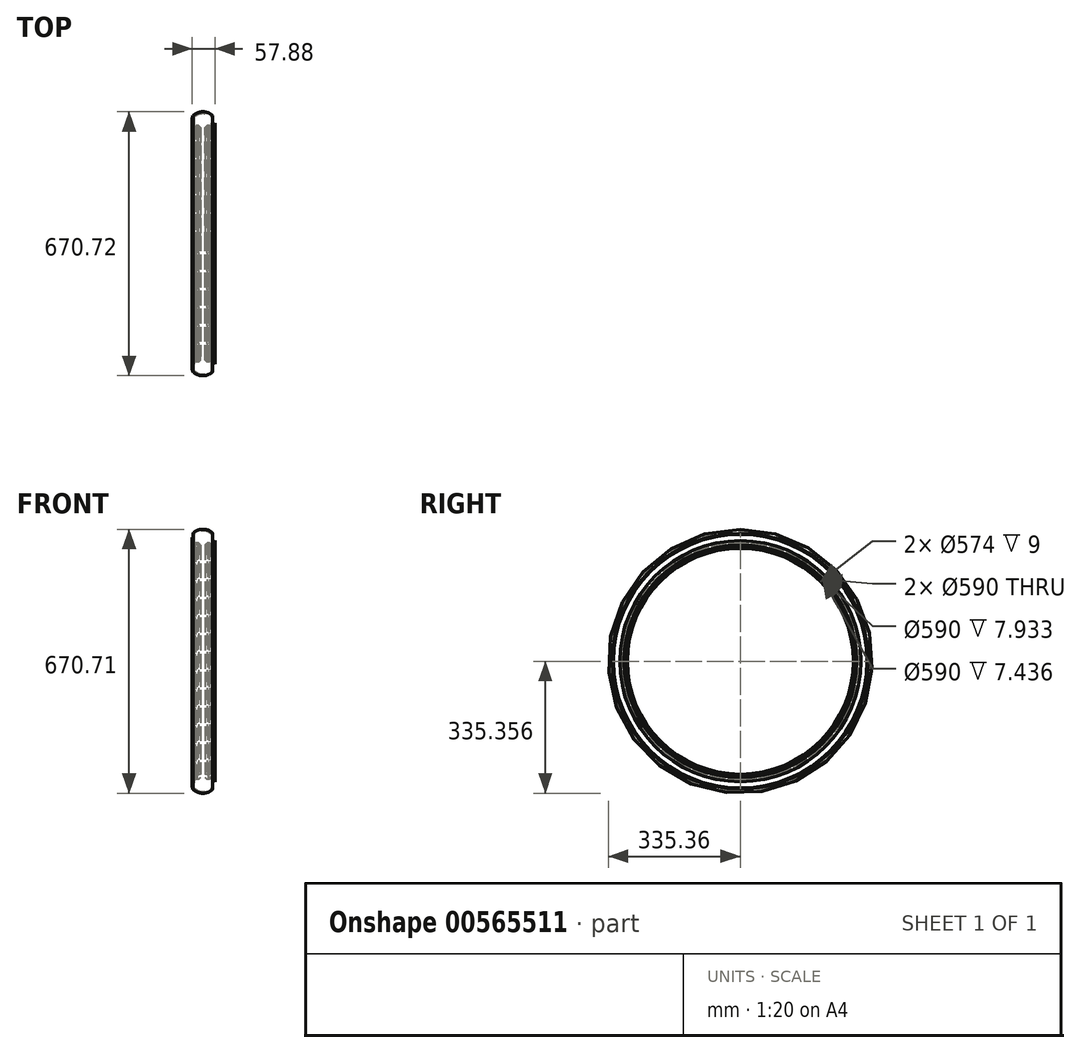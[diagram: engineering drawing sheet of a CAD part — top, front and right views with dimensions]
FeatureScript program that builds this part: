
annotation { "Feature Type Name" : "Feature", "Feature Type Description" : "" }
export const myFeature = defineFeature(function(context is Context, id is Id, definition is map)
    precondition{}
    {
        {
            var Q0;
            Q0=qCreatedBy(makeId("Front.planeOp"),FACE);
            var sketch = newSketch(context, id + "F0", { "sketchPlane" : qUnion([Q0])});
            skLineSegment(sketch, "E0", {"start": v(-253.23, -259.64) * mm, "end": v(-183.54, -259.64) * mm, "construction": true});
            skArc(sketch, "E1", {"start": v(-228.23, 65.36) * mm, "mid": v(-253.23, 75.71) * mm, "end": v(-278.23, 65.36) * mm});
            skLineSegment(sketch, "E2", {"start": v(-278.23, 65.36) * mm, "end": v(-228.23, 65.36) * mm, "construction": true});
            skLineSegment(sketch, "E3", {"start": v(-270.34, 40.36) * mm, "end": v(-264.23, 40.36) * mm});
            skLineSegment(sketch, "E4", {"start": v(-273.23, 35.36) * mm, "end": v(-265.23, 35.36) * mm});
            skLineSegment(sketch, "E5", {"start": v(-253.23, 40.36) * mm, "end": v(-253.23, 35.36) * mm, "construction": true});
            skArc(sketch, "E6.0", {"start": v(-231.06, 62.53) * mm, "mid": v(-253.23, 71.71) * mm, "end": v(-275.4, 62.53) * mm});
            skLineSegment(sketch, "E7", {"start": v(-231.06, 62.53) * mm, "end": v(-228.23, 65.36) * mm});
            skLineSegment(sketch, "E8", {"start": v(-231.06, 62.53) * mm, "end": v(-226.37, 57.84) * mm, "construction": true});
            skLineSegment(sketch, "E9.0.MirrorCS", {"start": v(-275.4, 62.53) * mm, "end": v(-278.23, 65.36) * mm});
            skLineSegment(sketch, "E10", {"start": v(-273.23, 35.36) * mm, "end": v(-270.34, 40.36) * mm});
            skPoint(sketch, "E11.start.orphan", {"position": v(-265.73, 40.36) * mm});
            skLineSegment(sketch, "E12", {"start": v(-265.23, 35.36) * mm, "end": v(-265.23, 30.36) * mm});
            skLineSegment(sketch, "E13", {"start": v(-265.23, 30.36) * mm, "end": v(-268.23, 30.36) * mm});
            skLineSegment(sketch, "E14", {"start": v(-268.23, 30.36) * mm, "end": v(-268.23, 27.36) * mm});
            skLineSegment(sketch, "E15", {"start": v(-268.23, 27.36) * mm, "end": v(-259.23, 27.36) * mm});
            skLineSegment(sketch, "E16", {"start": v(-259.23, 27.36) * mm, "end": v(-259.23, 35.36) * mm});
            skLineSegment(sketch, "E17", {"start": v(-259.23, 35.36) * mm, "end": v(-264.23, 40.36) * mm});
            skLineSegment(sketch, "E18.0.MirrorCS", {"start": v(-233.23, 35.36) * mm, "end": v(-236.11, 40.36) * mm});
            skLineSegment(sketch, "E18.1.MirrorCS", {"start": v(-241.23, 35.36) * mm, "end": v(-241.23, 30.36) * mm});
            skLineSegment(sketch, "E18.2.MirrorCS", {"start": v(-241.23, 30.36) * mm, "end": v(-238.23, 30.36) * mm});
            skPoint(sketch, "E18.3.MirrorP", {"position": v(-240.73, 40.36) * mm});
            skLineSegment(sketch, "E18.4.MirrorCS", {"start": v(-236.11, 40.36) * mm, "end": v(-242.23, 40.36) * mm});
            skLineSegment(sketch, "E18.5.MirrorCS", {"start": v(-238.23, 27.36) * mm, "end": v(-247.23, 27.36) * mm});
            skLineSegment(sketch, "E18.6.MirrorCS", {"start": v(-247.23, 35.36) * mm, "end": v(-242.23, 40.36) * mm});
            skLineSegment(sketch, "E18.7.MirrorCS", {"start": v(-238.23, 30.36) * mm, "end": v(-238.23, 27.36) * mm});
            skLineSegment(sketch, "E18.8.MirrorCS", {"start": v(-247.23, 27.36) * mm, "end": v(-247.23, 35.36) * mm});
            skLineSegment(sketch, "E19.0.MirrorCS", {"start": v(-233.23, 35.36) * mm, "end": v(-241.23, 35.36) * mm});
            skSolve(sketch);
        }
        {
            var Q0;
            Q0=makeQuery(id+"F0.imprint","IMPRINT",FACE,{"disambiguationData":[TD([[makeQuery(id+"F0.imprint","IMPRINT",EDGE,{"derivedFrom":sQuery(id+"F0.wireOp",EDGE,"E1")}),1.0]])]});
            var Q1;
            Q1=makeQuery(id+"F0.imprint","IMPRINT",FACE,{"disambiguationData":[TD([[makeQuery(id+"F0.imprint","IMPRINT",EDGE,{"derivedFrom":sQuery(id+"F0.wireOp",EDGE,"E18.0.MirrorCS")}),1.0]])]});
            var Q2;
            Q2=makeQuery(id+"F0.imprint","IMPRINT",FACE,{"disambiguationData":[TD([[makeQuery(id+"F0.imprint","IMPRINT",EDGE,{"derivedFrom":sQuery(id+"F0.wireOp",EDGE,"E3")}),-1.0]])]});
            var Q3;
            Q3=sQuery(id+"F0.wireOp",EDGE,"E0");
            revolve(context, id + "F1", {"entities" : qUnion([Q0, Q1, Q2]), "axis" : qUnion([Q3]), "revolveType" : RevolveType.FULL});
        }
        {
            var Q0;
            Q0=qCreatedBy(makeId("Front.planeOp"),FACE);
            var sketch = newSketch(context, id + "F2", { "sketchPlane" : qUnion([Q0])});
            skArc(sketch, "E20", {"start": v(-233.83, 35.31) * mm, "mid": v(-222.2, 49.33) * mm, "end": v(-228.35, 66.47) * mm});
            skLineSegment(sketch, "E21", {"start": v(-233.83, 35.31) * mm, "end": v(-237.09, 41.01) * mm});
            skLineSegment(sketch, "E22.0", {"start": v(-353.64, -481.88) * mm, "end": v(-353.64, -476.88) * mm});
            skLineSegment(sketch, "E23", {"start": v(-358.7, 140.29) * mm, "end": v(-278.63, 66.47) * mm});
            skArc(sketch, "E24", {"start": v(-278.63, 66.47) * mm, "mid": v(-280.33, 50.11) * mm, "end": v(-273.15, 35.31) * mm});
            skArc(sketch, "E25", {"start": v(-358.7, 140.29) * mm, "mid": v(-359.62, 128.41) * mm, "end": v(-353.64, 118.12) * mm});
            skPoint(sketch, "E26.orphan", {"position": v(-273.15, 35.31) * mm});
            skPoint(sketch, "E27.orphan", {"position": v(-253.5, -297.81) * mm});
            skLineSegment(sketch, "E28", {"start": v(-253.5, -297.81) * mm, "end": v(-222.8, -297.81) * mm, "construction": true});
            skLineSegment(sketch, "E29", {"start": v(-253.5, 75.58) * mm, "end": v(-253.5, -297.81) * mm, "construction": true});
            skLineSegment(sketch, "E30", {"start": v(-273.15, 35.31) * mm, "end": v(-353.64, 118.12) * mm});
            skLineSegment(sketch, "E31.0.MirrorCS", {"start": v(-148.29, 140.29) * mm, "end": v(-228.35, 66.47) * mm});
            skArc(sketch, "E32.0.MirrorCS", {"start": v(-228.35, 66.47) * mm, "mid": v(-226.65, 50.11) * mm, "end": v(-233.83, 35.31) * mm});
            skLineSegment(sketch, "E33.0.MirrorCS", {"start": v(-233.83, 35.31) * mm, "end": v(-153.35, 118.12) * mm});
            skArc(sketch, "E34.0.MirrorCS", {"start": v(-148.29, 140.29) * mm, "mid": v(-147.36, 128.41) * mm, "end": v(-153.35, 118.12) * mm});
            skArc(sketch, "E35", {"start": v(-278.63, 66.47) * mm, "mid": v(-276.42, 50.8) * mm, "end": v(-273.15, 35.31) * mm});
            skSolve(sketch);
        }
        {
            var Q0;
            Q0=makeQuery(id+"F2.imprint","IMPRINT",FACE,{"disambiguationData":[TD([[makeQuery(id+"F2.imprint","IMPRINT",EDGE,{"derivedFrom":sQuery(id+"F2.wireOp",EDGE,"E24")}),1.0]])]});
            var Q1;
            {var subQ0=sQuery(id+"F2.wireOp",EDGE,"E32.0.MirrorCS");Q1=makeQuery(id+"F2.imprint","IMPRINT",FACE,{"disambiguationData":[TD([[makeQuery(id+"F2.imprint","IMPRINT",EDGE,{"derivedFrom":subQ0}),1.0]])]});}
            var Q2;
            {var subQ0=sQuery(id+"F2.wireOp",EDGE,"E33.0.MirrorCS");var subQ1=sQuery(id+"F2.wireOp",EDGE,"E20");var subQ3=makeQuery(id+"F2.imprint","INTERSECT",VERTEX,{"derivedFrom":[subQ1,subQ0]});Q2=makeQuery(id+"F2.imprint","IMPRINT",FACE,{"disambiguationData":[TD([[makeQuery(id+"F2.imprint","IMPRINT",EDGE,{"disambiguationData":[TD([[subQ3,1.0]])],"derivedFrom":subQ1}),1.0]])]});}
            var Q3;
            Q3=sQuery(id+"F0.wireOp",EDGE,"E0");
            revolve(context, id + "F3", {"operationType" : NewBodyOperationType.ADD, "entities" : qUnion([Q0, Q1, Q2]), "axis" : qUnion([Q3]), "revolveType" : RevolveType.FULL});
        }
    });
